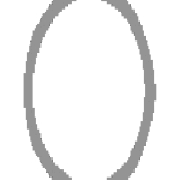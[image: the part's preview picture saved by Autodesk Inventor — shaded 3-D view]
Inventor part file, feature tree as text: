
AUTODESK INVENTOR PART (.ipt)
format: ipt  version: 2021 (Build 250183000, 183)  size: 112,128 bytes
history: native  units: in
note: dims shown in document units (in); Inventor stores cm internally (conversion verified against a paired STEP export)
features: other x4, sketch x3, plane x1
ambient origin geometry x8: Origin, YZ Plane, XZ Plane, XY Plane, X Axis, Y Axis, Z Axis, Center Point
bodies: Solid1 (feature_tree), Body (feature_tree)
feature tree (8):
  other  "Driven Length"
  other  "Frame Generator"
  other  "Start Plane"
  other  "End Plane"
  sketch  "Sketch"  dims[d2=19.6468in d4=-0.0in d5=19.6468in d6=0.12in d7=0.0in d8=90.0deg d9=19.6468in]
  sketch  "Sketch2"  dims[d0=1.0in]
  plane  "Work Plane3"
  sketch  "Sketch3"  dims[d1=0.065in]
